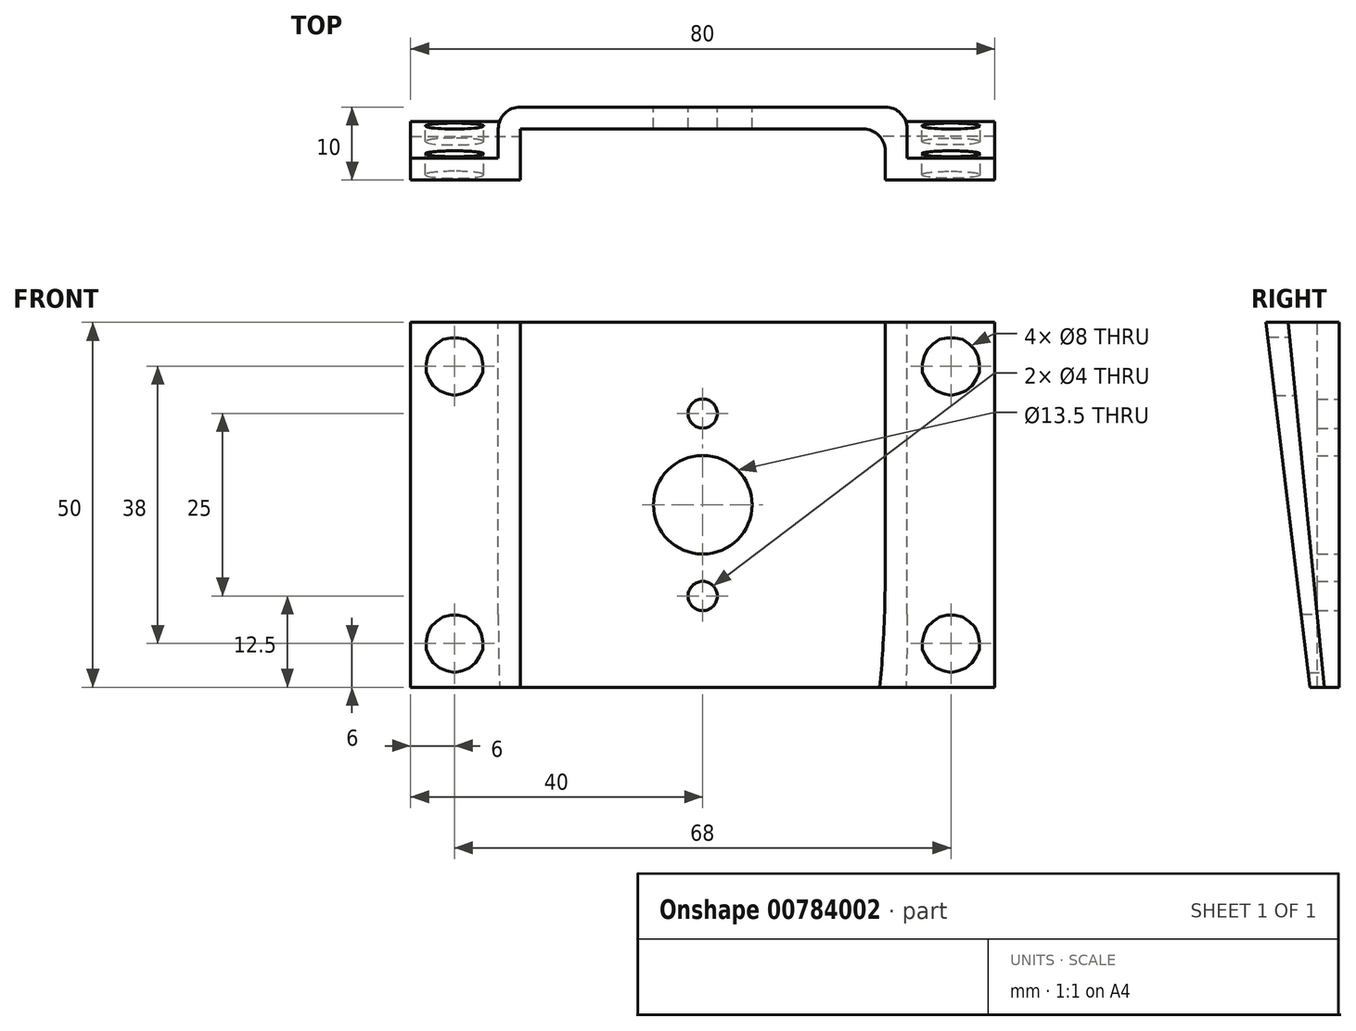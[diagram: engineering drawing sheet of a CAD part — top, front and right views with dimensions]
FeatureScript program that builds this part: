
annotation { "Feature Type Name" : "Feature", "Feature Type Description" : "" }
export const myFeature = defineFeature(function(context is Context, id is Id, definition is map)
    precondition{}
    {
        {
            var Q0;
            Q0=qCreatedBy(makeId("Front.planeOp"),FACE);
            var sketch = newSketch(context, id + "F0", { "sketchPlane" : qUnion([Q0])});
            skLineSegment(sketch, "E0.bottom", {"start": v(-25, -25) * mm, "end": v(25, -25) * mm});
            skLineSegment(sketch, "E0.top", {"start": v(-25, 25) * mm, "end": v(25, 25) * mm});
            skLineSegment(sketch, "E0.left", {"start": v(-25, -25) * mm, "end": v(-25, 25) * mm});
            skLineSegment(sketch, "E0.right", {"start": v(25, -25) * mm, "end": v(25, 25) * mm});
            skPoint(sketch, "E0.middle", {"position": v(0, 0) * mm});
            skCircle(sketch, "E1", {"center": v(0, 0) * mm, "radius": 6.75 * mm});
            skLineSegment(sketch, "E2", {"start": v(-25, 25) * mm, "end": v(-25, -25) * mm});
            skPoint(sketch, "E3", {"position": v(0, 12.5) * mm});
            skPoint(sketch, "E4", {"position": v(0, -12.5) * mm});
            skCircle(sketch, "E5", {"center": v(0, 12.5) * mm, "radius": 2 * mm});
            skCircle(sketch, "E6", {"center": v(0, -12.5) * mm, "radius": 2 * mm});
            skSolve(sketch);
        }
        {
            var Q0;
            Q0=qSketchRegion(id+"F0",true);
            extrude(context, id + "F1", {"entities" : qUnion([Q0]), "depth" : 3 * mm, "offsetDistance" : 25 * mm});
        }
        {
            var Q0;
            Q0=qCreatedBy(makeId("Right.planeOp"),FACE);
            var sketch = newSketch(context, id + "F2", { "sketchPlane" : qUnion([Q0])});
            skLineSegment(sketch, "E7", {"start": v(-2, 25) * mm, "end": v(0, 25) * mm});
            skLineSegment(sketch, "E8", {"start": v(0, 25) * mm, "end": v(0, -25) * mm});
            skLineSegment(sketch, "E9", {"start": v(0, -25) * mm, "end": v(-2, -25) * mm});
            skLineSegment(sketch, "E10", {"start": v(-2, -25) * mm, "end": v(-7, 25) * mm});
            skLineSegment(sketch, "E11", {"start": v(-7, 25) * mm, "end": v(-2, 25) * mm});
            skSolve(sketch);
        }
        {
            var Q0;
            Q0=makeQuery(id+"F2.imprint","IMPRINT",FACE,{"disambiguationData":[TD([[makeQuery(id+"F2.imprint","IMPRINT",EDGE,{"derivedFrom":sQuery(id+"F2.wireOp",EDGE,"E7")}),-1.0]])]});
            extrude(context, id + "F3", {"entities" : qUnion([Q0]), "operationType" : NewBodyOperationType.ADD, "depth" : 28 * mm, "offsetDistance" : 25 * mm, "hasSecondDirection" : true, "secondDirectionOppositeDirection" : false, "secondDirectionDepth" : 25 * mm});
        }
        {
            var Q0;
            Q0=qCreatedBy(makeId("Right.planeOp"),FACE);
            var sketch = newSketch(context, id + "F4", { "sketchPlane" : qUnion([Q0])});
            skLineSegment(sketch, "E12", {"start": v(0, 25) * mm, "end": v(-2, 25) * mm});
            skLineSegment(sketch, "E13", {"start": v(-2, 25) * mm, "end": v(-7, 25) * mm});
            skLineSegment(sketch, "E14", {"start": v(-7, 25) * mm, "end": v(-2, -25) * mm});
            skLineSegment(sketch, "E15", {"start": v(-2, -25) * mm, "end": v(0, -25) * mm});
            skLineSegment(sketch, "E16", {"start": v(0, -25) * mm, "end": v(0, 25) * mm});
            skSolve(sketch);
        }
        {
            var Q0;
            Q0=makeQuery(id+"F4.imprint","IMPRINT",FACE,{"disambiguationData":[TD([[makeQuery(id+"F4.imprint","IMPRINT",EDGE,{"derivedFrom":sQuery(id+"F4.wireOp",EDGE,"E12")}),1.0]])]});
            extrude(context, id + "F5", {"entities" : qUnion([Q0]), "operationType" : NewBodyOperationType.ADD, "oppositeDirection" : true, "depth" : 28 * mm, "offsetDistance" : 25 * mm, "hasSecondDirection" : true, "secondDirectionOppositeDirection" : true, "secondDirectionDepth" : 25 * mm});
        }
        {
            var Q0;
            Q0=qCreatedBy(makeId("Right.planeOp"),FACE);
            var sketch = newSketch(context, id + "F6", { "sketchPlane" : qUnion([Q0])});
            skLineSegment(sketch, "E17", {"start": v(-7, 25) * mm, "end": v(-2, -25) * mm});
            skLineSegment(sketch, "E18", {"start": v(-2, -25) * mm, "end": v(-4, -25) * mm});
            skLineSegment(sketch, "E19", {"start": v(-4, -25) * mm, "end": v(-10, 25) * mm});
            skLineSegment(sketch, "E20", {"start": v(-10, 25) * mm, "end": v(-7, 25) * mm});
            skSolve(sketch);
        }
        {
            var Q0;
            Q0=qSketchRegion(id+"F6",true);
            extrude(context, id + "F7", {"entities" : qUnion([Q0]), "operationType" : NewBodyOperationType.ADD, "depth" : 40 * mm, "offsetDistance" : 25 * mm, "hasSecondDirection" : true, "secondDirectionOppositeDirection" : false, "secondDirectionDepth" : 25 * mm});
        }
        {
            var Q0;
            Q0=qSketchRegion(id+"F6",true);
            extrude(context, id + "F8", {"entities" : qUnion([Q0]), "operationType" : NewBodyOperationType.ADD, "oppositeDirection" : true, "depth" : 40 * mm, "offsetDistance" : 25 * mm, "hasSecondDirection" : true, "secondDirectionOppositeDirection" : true, "secondDirectionDepth" : 25 * mm});
        }
        {
            var Q0;
            Q0=qCreatedBy(makeId("Front.planeOp"),FACE);
            var sketch = newSketch(context, id + "F9", { "sketchPlane" : qUnion([Q0])});
            skPoint(sketch, "E21", {"position": v(-34, 19) * mm});
            skPoint(sketch, "E22", {"position": v(-34, -19) * mm});
            skPoint(sketch, "E23", {"position": v(34, -19) * mm});
            skPoint(sketch, "E24", {"position": v(34, 19) * mm});
            skSolve(sketch);
        }
        {
            var Q0;
            Q0=sQuery(id+"F9.wireOp",VERTEX,"E21");
            var Q1;
            Q1=sQuery(id+"F9.wireOp",VERTEX,"E22");
            var Q2;
            Q2=sQuery(id+"F9.wireOp",VERTEX,"E23");
            var Q3;
            Q3=sQuery(id+"F9.wireOp",VERTEX,"E24");
            var Q4;
            Q4=makeQuery(id+"F1.opExtrude","SWEPT_BODY",BODY,{"disambiguationData":[OSD([sQuery(id+"F0.wireOp",EDGE,"E0.bottom"),sQuery(id+"F0.wireOp",EDGE,"E0.top"),sQuery(id+"F0.wireOp",EDGE,"E0.right"),sQuery(id+"F0.wireOp",EDGE,"E1"),sQuery(id+"F0.wireOp",EDGE,"MAszpG2d-Ajmr-m0A9-8idj-gPqS8RMXXwU3"),sQuery(id+"F0.wireOp",EDGE,"ec558718-f26b-4aae-9179-19d8661be785.1.0"),sQuery(id+"F0.wireOp",EDGE,"ec558718-f26b-4aae-9179-19d8661be785.2.0"),sQuery(id+"F0.wireOp",EDGE,"E2")])]});
            hole(context, id + "F10", {"style" : HoleStyle.SIMPLE, "endStyle" : HoleEndStyle.THROUGH, "oppositeDirection" : true, "holeDiameter" : 8 * mm, "majorDiameter" : 5 * mm, "isTappedThrough" : true, "tappedDepth" : 12 * mm, "tapClearance" : 3, "locations" : qUnion([Q0, Q1, Q2, Q3]), "scope" : qUnion([Q4])});
        }
        {
            var Q0;
            Q0=makeQuery(id+"F5.opExtrude","CAP_EDGE",EDGE,{"disambiguationData":[OSD([sQuery(id+"F4.wireOp",EDGE,"E16")])],"isStart":false});
            var Q1;
            Q1=makeQuery(id+"F3.opExtrude","CAP_EDGE",EDGE,{"disambiguationData":[OSD([sQuery(id+"F2.wireOp",EDGE,"E8")])],"isStart":false});
            var Q2;
            Q2=makeQuery(id+"F1.opExtrude","CAP_EDGE",EDGE,{"disambiguationData":[OSD([sQuery(id+"F0.wireOp",EDGE,"E0.right")])],"isStart":false});
            var Q3;
            Q3=makeQuery(id+"F1.opExtrude","CAP_EDGE",EDGE,{"disambiguationData":[OSD([sQuery(id+"F0.wireOp",EDGE,"E2")])],"isStart":false});
            fillet(context, id + "F11", {"entities" : qUnion([Q0, Q1, Q2, Q3]), "radius" : 3 * mm, "tangentPropagation" : true, "defaultsChanged" : false, "vertexSettings" : [], "allowEdgeOverflow" : false});
        }
    });
